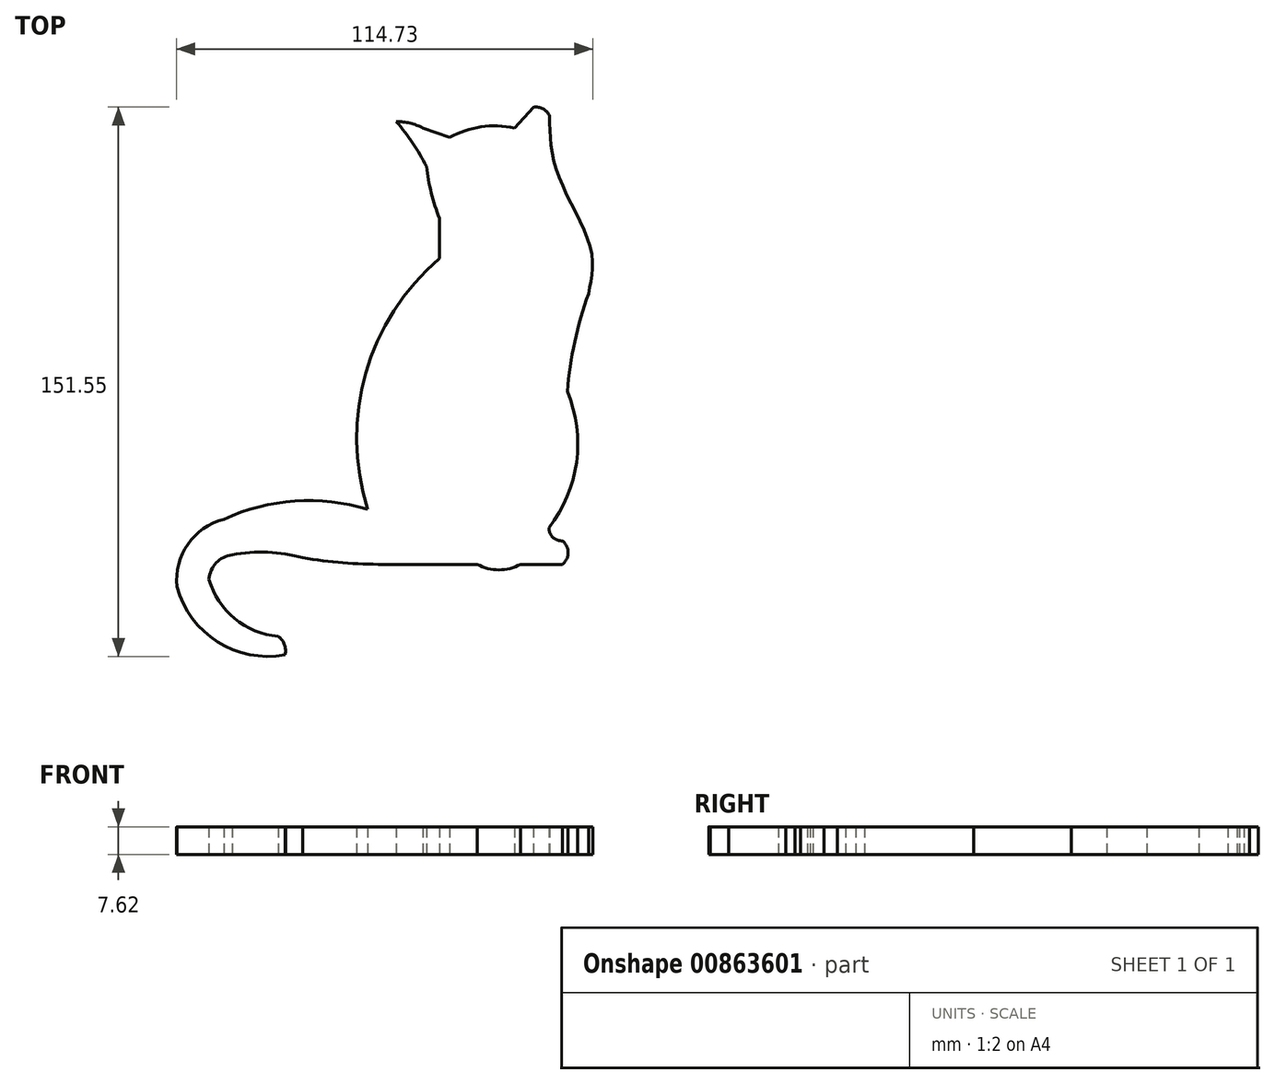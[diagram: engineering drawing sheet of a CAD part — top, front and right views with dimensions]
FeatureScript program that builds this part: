
annotation { "Feature Type Name" : "Feature", "Feature Type Description" : "" }
export const myFeature = defineFeature(function(context is Context, id is Id, definition is map)
    precondition{}
    {
        {
            var Q0;
            Q0=qCreatedBy(makeId("Top.planeOp"),FACE);
            var sketch = newSketch(context, id + "F0", { "sketchPlane" : qUnion([Q0])});
            skLineSegment(sketch, "E0", {"start": v(17.8, 70.3) * mm, "end": v(23.1, 76) * mm});
            skPoint(sketch, "E0.startSnap0", {"position": v(-7.37, 70.3) * mm});
            skLineSegment(sketch, "E1", {"start": v(7.58, -50.1) * mm, "end": v(-18.32, -50.1) * mm});
            skLineSegment(sketch, "E2", {"start": v(19.51, -50.1) * mm, "end": v(31.1, -50.1) * mm});
            skArc(sketch, "E3", {"start": v(-6.4, 59.65) * mm, "mid": v(-5.08, 52.37) * mm, "end": v(-2.81, 45.33) * mm});
            skArc(sketch, "E4", {"start": v(-2.81, 34.25) * mm, "mid": v(-23.18, 2.66) * mm, "end": v(-22.58, -34.94) * mm});
            skLineSegment(sketch, "E5", {"start": v(-2.81, 45.33) * mm, "end": v(-2.81, 41.75) * mm});
            skLineSegment(sketch, "E6", {"start": v(-2.81, 41.75) * mm, "end": v(-2.81, 34.25) * mm});
            skArc(sketch, "E7", {"start": v(27.52, 73.62) * mm, "mid": v(25.71, 75.57) * mm, "end": v(23.1, 76) * mm});
            skFitSpline(sketch, "E8", {"points": [v(27.52, 73.62) * mm, v(29.64, 58.01) * mm, v(38.98, 36.44) * mm, v(38.28, 24.57) * mm], "startDerivative": vector(0.64, -45.79) * mm, "endDerivative": vector(-7.23, -39.07) * mm});
            skArc(sketch, "E9", {"start": v(38.28, 24.57) * mm, "mid": v(34.46, 11.29) * mm, "end": v(32.46, -2.39) * mm});
            skArc(sketch, "E10", {"start": v(27.35, -40.05) * mm, "mid": v(34.96, -21.9) * mm, "end": v(32.46, -2.39) * mm});
            skArc(sketch, "E11", {"start": v(27.35, -40.05) * mm, "mid": v(28.46, -42.64) * mm, "end": v(31.1, -43.63) * mm});
            skArc(sketch, "E12", {"start": v(-22.58, -34.94) * mm, "mid": v(-42.68, -32.65) * mm, "end": v(-62.29, -37.66) * mm});
            skArc(sketch, "E13", {"start": v(-62.29, -37.66) * mm, "mid": v(-72.22, -44.54) * mm, "end": v(-75.24, -56.24) * mm});
            skArc(sketch, "E14", {"start": v(-75.24, -56.24) * mm, "mid": v(-64.02, -71.48) * mm, "end": v(-45.43, -75.06) * mm});
            skArc(sketch, "E15", {"start": v(-45.43, -75.06) * mm, "mid": v(-45.58, -72.2) * mm, "end": v(-47.34, -69.94) * mm});
            skArc(sketch, "E16", {"start": v(-66.4, -54.2) * mm, "mid": v(-59.32, -65.05) * mm, "end": v(-47.34, -69.94) * mm});
            skArc(sketch, "E17", {"start": v(-60, -47.46) * mm, "mid": v(-64.4, -49.7) * mm, "end": v(-66.4, -54.2) * mm});
            skArc(sketch, "E18", {"start": v(-40.49, -48.3) * mm, "mid": v(-50.2, -46.77) * mm, "end": v(-60, -47.46) * mm});
            skArc(sketch, "E19", {"start": v(-40.49, -48.3) * mm, "mid": v(-29.44, -49.65) * mm, "end": v(-18.32, -50.1) * mm});
            skArc(sketch, "E20", {"start": v(7.58, -50.1) * mm, "mid": v(13.55, -51.62) * mm, "end": v(19.51, -50.1) * mm});
            skPoint(sketch, "E21.start.orphan", {"position": v(-14.74, 72.09) * mm});
            skArc(sketch, "E22", {"start": v(-7.37, 70.3) * mm, "mid": v(-10.95, 71.61) * mm, "end": v(-14.74, 72.09) * mm});
            skArc(sketch, "E23", {"start": v(-6.4, 59.65) * mm, "mid": v(-10.21, 66.1) * mm, "end": v(-14.74, 72.09) * mm});
            skPoint(sketch, "E24.end.orphan", {"position": v(0, 68.5) * mm});
            skLineSegment(sketch, "E25", {"start": v(-7.37, 70.3) * mm, "end": v(0, 67.66) * mm});
            skArc(sketch, "E26", {"start": v(17.8, 70.3) * mm, "mid": v(8.66, 70.6) * mm, "end": v(0, 67.66) * mm});
            skArc(sketch, "E27", {"start": v(31.1, -50.1) * mm, "mid": v(32.65, -46.86) * mm, "end": v(31.1, -43.63) * mm});
            skSolve(sketch);
        }
        {
            var Q0;
            Q0 = qSketchRegion(id + "F0", true);
            extrude(context, id + "F1", {"entities" : qUnion([Q0]), "depth" : 7.62 * mm, "offsetDistance" : 25.4 * mm});
        }
    });
